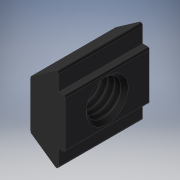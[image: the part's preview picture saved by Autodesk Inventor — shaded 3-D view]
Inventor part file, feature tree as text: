
AUTODESK INVENTOR PART (.ipt)
format: ipt  version: 2019 (Build 230136000, 136)  size: 152,064 bytes
history: native  units: mm
features: other x28, sketch x2, extrude x1, revolve x1, thread x1
ambient origin geometry x8: Origin, YZ Plane, XZ Plane, XY Plane, X Axis, Y Axis, Z Axis, Center Point
bodies: Solid1 (feature_tree)
feature tree (33):
  extrude  "Extrusion1"  TaperAngle=360.0deg  [1 undecoded]
  revolve  "Revolution1"  [1 undecoded]
  thread  "Thread1"  [1 undecoded]
  other  "nut_XY"
  other  "nut_YZ"
  other  "nut_ZX"
  other  "nut_X"
  other  "nut_Y"
  other  "nut_Z"
  other  "nut_Center"
  other  "to_bolt_XY"
  other  "to_bolt_YZ"
  other  "to_bolt_ZX"
  other  "to_bolt_X"
  other  "to_bolt_Y"
  other  "to_bolt_Z"
  other  "to_bolt_Center"
  other  "to_frames_XY"
  other  "to_frames_YZ"
  other  "to_frames_ZX"
  other  "to_frames_X"
  other  "to_frames_Y"
  other  "to_frames_Z"
  other  "to_frames_Center"
  other  "to_lane_XY"
  other  "to_lane_YZ"
  other  "to_lane_ZX"
  other  "to_lane_X"
  other  "to_lane_Y"
  other  "to_lane_Z"
  other  "to_lane_Center"
  sketch  "Sketch_2"  dims[d0=10.0mm d1=0.0mm d2=360.0deg]
  sketch  "Sketch_5"  dims[d3=3.234mm d4=0.0mm d5=0.0mm d6=0.0mm]
note: 3 required parameter values undecoded (feature->parameter linkage not recoverable at this tier; creation-order binding heuristic only, values carry confidence <= 0.55)